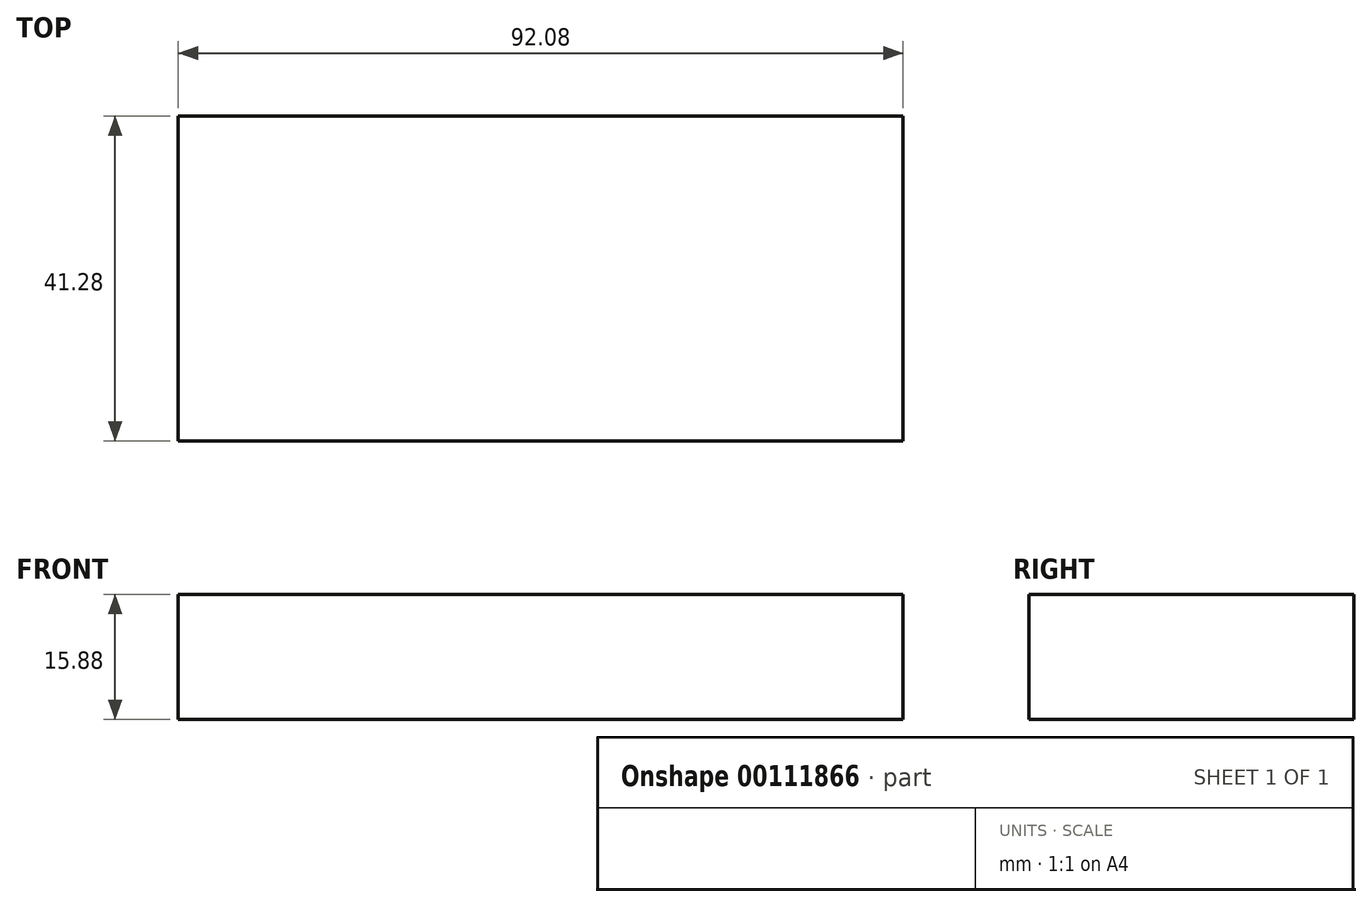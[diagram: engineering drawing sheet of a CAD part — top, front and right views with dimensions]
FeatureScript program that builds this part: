
annotation { "Feature Type Name" : "Feature", "Feature Type Description" : "" }
export const myFeature = defineFeature(function(context is Context, id is Id, definition is map)
    precondition{}
    {
        {
            var Q0;
            Q0=qCreatedBy(makeId("Top.planeOp"),FACE);
            var sketch = newSketch(context, id + "F0", { "sketchPlane" : qUnion([Q0])});
            skLineSegment(sketch, "E0.bottom", {"start": v(46.04, 20.64) * mm, "end": v(-46.04, 20.64) * mm});
            skLineSegment(sketch, "E0.top", {"start": v(46.04, -20.64) * mm, "end": v(-46.04, -20.64) * mm});
            skLineSegment(sketch, "E0.left", {"start": v(46.04, 20.64) * mm, "end": v(46.04, -20.64) * mm});
            skLineSegment(sketch, "E0.right", {"start": v(-46.04, 20.64) * mm, "end": v(-46.04, -20.64) * mm});
            skPoint(sketch, "E0.middle", {"position": v(0, 0) * mm});
            skSolve(sketch);
        }
        {
            var Q0;
            Q0=makeQuery(id+"F0.imprint","IMPRINT",FACE,{"disambiguationData":[TD([[makeQuery(id+"F0.imprint","IMPRINT",EDGE,{"derivedFrom":sQuery(id+"F0.wireOp",EDGE,"E0.bottom")}),1.0]])]});
            extrude(context, id + "F1", {"entities" : qUnion([Q0]), "oppositeDirection" : true, "depth" : 15.88 * mm});
        }
    });
